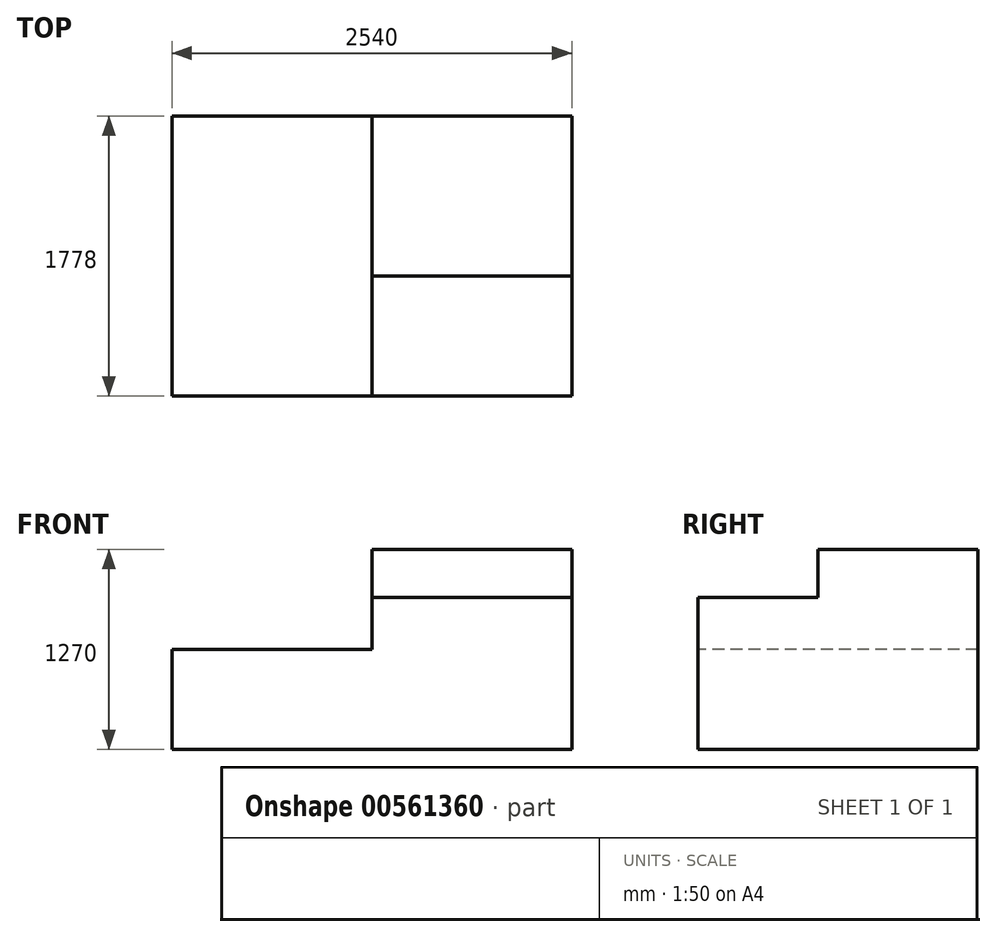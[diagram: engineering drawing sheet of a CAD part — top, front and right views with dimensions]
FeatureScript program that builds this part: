
annotation { "Feature Type Name" : "Feature", "Feature Type Description" : "" }
export const myFeature = defineFeature(function(context is Context, id is Id, definition is map)
    precondition{}
    {
        {
            var Q0;
            Q0=qCreatedBy(makeId("Front.planeOp"),FACE);
            var sketch = newSketch(context, id + "F0", { "sketchPlane" : qUnion([Q0])});
            skLineSegment(sketch, "E0.bottom", {"start": v(0, 0) * mm, "end": v(2540, 0) * mm});
            skLineSegment(sketch, "E0.top", {"start": v(0, 1270) * mm, "end": v(2540, 1270) * mm});
            skLineSegment(sketch, "E0.left", {"start": v(0, 0) * mm, "end": v(0, 1270) * mm});
            skLineSegment(sketch, "E0.right", {"start": v(2540, 0) * mm, "end": v(2540, 1270) * mm});
            skSolve(sketch);
        }
        {
            var Q0;
            Q0=makeQuery(id+"F0.imprint","IMPRINT",FACE,{"disambiguationData":[TD([[makeQuery(id+"F0.imprint","IMPRINT",EDGE,{"derivedFrom":sQuery(id+"F0.wireOp",EDGE,"E0.bottom")}),1.0]])]});
            extrude(context, id + "F1", {"entities" : qUnion([Q0]), "depth" : 1778 * mm, "offsetDistance" : 25.4 * mm});
        }
        {
            var Q0;
            Q0=makeQuery(id+"F1.opExtrude","CAP_FACE",FACE,{"disambiguationData":[OSD([sQuery(id+"F0.wireOp",EDGE,"E0.bottom"),sQuery(id+"F0.wireOp",EDGE,"E0.top"),sQuery(id+"F0.wireOp",EDGE,"E0.left"),sQuery(id+"F0.wireOp",EDGE,"E0.right")])],"isStart":false});
            var sketch = newSketch(context, id + "F2", { "sketchPlane" : qUnion([Q0])});
            skLineSegment(sketch, "E1", {"start": v(2540, 965.2) * mm, "end": v(1270, 965.2) * mm});
            skLineSegment(sketch, "E2", {"start": v(1270, 965.2) * mm, "end": v(1270, 1270) * mm});
            skSolve(sketch);
        }
        {
            var Q0;
            {var subQ0=sQuery(id+"F2.wireOp",EDGE,"E1");Q0=makeQuery(id+"F2.imprint","IMPRINT",FACE,{"disambiguationData":[TD([[makeQuery(id+"F2.imprint","IMPRINT",EDGE,{"derivedFrom":subQ0}),-1.0]])]});}
            extrude(context, id + "F3", {"entities" : qUnion([Q0]), "operationType" : NewBodyOperationType.REMOVE, "oppositeDirection" : true, "depth" : 762 * mm, "offsetDistance" : 25.4 * mm});
        }
        {
            var Q0;
            Q0=makeQuery(id+"F1.opExtrude","CAP_FACE",FACE,{"disambiguationData":[OSD([sQuery(id+"F0.wireOp",EDGE,"E0.bottom"),sQuery(id+"F0.wireOp",EDGE,"E0.top"),sQuery(id+"F0.wireOp",EDGE,"E0.left"),sQuery(id+"F0.wireOp",EDGE,"E0.right")])],"isStart":false});
            var sketch = newSketch(context, id + "F4", { "sketchPlane" : qUnion([Q0])});
            skLineSegment(sketch, "E3", {"start": v(1270, 965.2) * mm, "end": v(1270, 635) * mm});
            skLineSegment(sketch, "E4", {"start": v(1270, 635) * mm, "end": v(0, 635) * mm});
            skSolve(sketch);
        }
        {
            var Q0;
            Q0=makeQuery(id+"F4.imprint","IMPRINT",FACE,{"disambiguationData":[TD([[makeQuery(id+"F4.imprint","IMPRINT",EDGE,{"derivedFrom":sQuery(id+"F4.wireOp",EDGE,"E3")}),-1.0]])]});
            extrude(context, id + "F5", {"entities" : qUnion([Q0]), "operationType" : NewBodyOperationType.REMOVE, "oppositeDirection" : true, "depth" : 1778 * mm, "offsetDistance" : 25.4 * mm});
        }
    });
